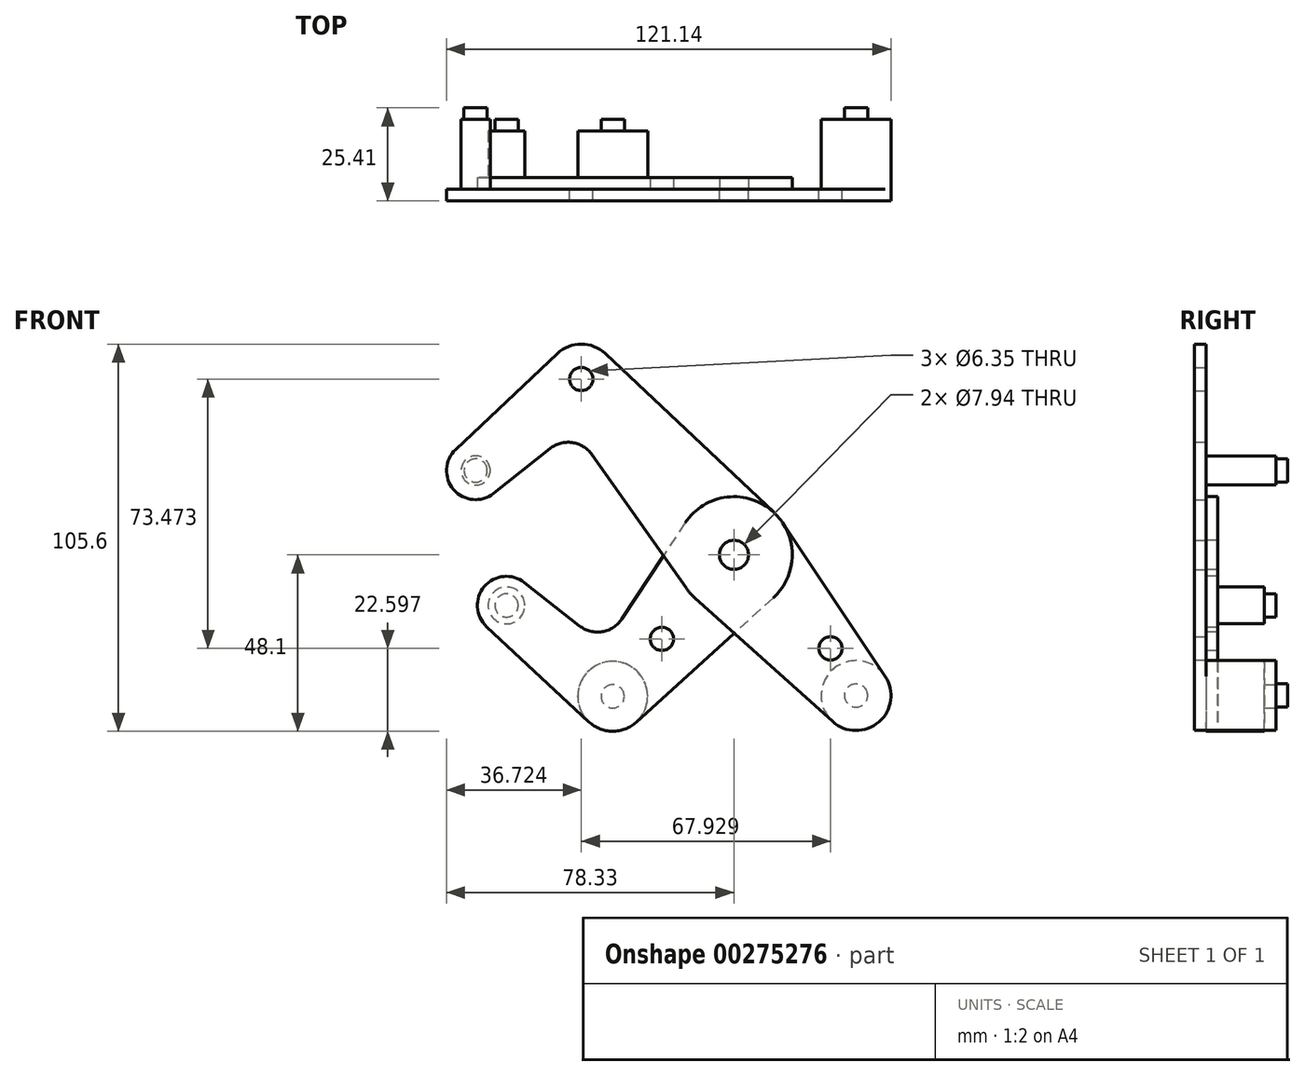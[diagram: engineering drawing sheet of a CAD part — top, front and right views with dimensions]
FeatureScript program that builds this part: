
annotation { "Feature Type Name" : "Feature", "Feature Type Description" : "" }
export const myFeature = defineFeature(function(context is Context, id is Id, definition is map)
    precondition{}
    {
        {
            var Q0;
            Q0=qCreatedBy(makeId("Front.planeOp"),FACE);
            var sketch = newSketch(context, id + "F0", { "sketchPlane" : qUnion([Q0])});
            skLineSegment(sketch, "E0", {"start": v(-41.6, 47.97) * mm, "end": v(41.6, -47.97) * mm, "construction": true});
            skCircle(sketch, "E1", {"center": v(0, 0) * mm, "radius": 3.18 * mm});
            skCircle(sketch, "E2", {"center": v(33.29, -38.38) * mm, "radius": 3.18 * mm});
            skCircle(sketch, "E3", {"center": v(-41.6, 47.97) * mm, "radius": 3.18 * mm});
            skCircle(sketch, "E4", {"center": v(-70.39, 23) * mm, "radius": 3.18 * mm});
            skLineSegment(sketch, "E5", {"start": v(-41.6, 47.97) * mm, "end": v(-70.39, 23) * mm, "construction": true});
            skCircle(sketch, "E6", {"center": v(33.29, -38.38) * mm, "radius": 9.53 * mm});
            skCircle(sketch, "E7", {"center": v(-70.39, 23) * mm, "radius": 7.94 * mm});
            skCircle(sketch, "E8", {"center": v(-41.6, 47.97) * mm, "radius": 9.53 * mm});
            skLineSegment(sketch, "E9", {"start": v(-75.83, 28.78) * mm, "end": v(-48.14, 54.9) * mm});
            skLineSegment(sketch, "E10", {"start": v(-65.44, 16.8) * mm, "end": v(-50.15, 28.98) * mm});
            skCircle(sketch, "E11", {"center": v(0, 0) * mm, "radius": 15.88 * mm});
            skLineSegment(sketch, "E12", {"start": v(-35.07, 54.9) * mm, "end": v(10.9, 11.55) * mm});
            skLineSegment(sketch, "E13", {"start": v(-38.72, 27.35) * mm, "end": v(-12.97, -9.15) * mm});
            skLineSegment(sketch, "E14", {"start": v(-10.6, -11.82) * mm, "end": v(26.93, -45.47) * mm});
            skLineSegment(sketch, "E15", {"start": v(13.2, 8.82) * mm, "end": v(41.2, -33.08) * mm});
            skArc(sketch, "E16.filletArc", {"start": v(-38.72, 27.35) * mm, "mid": v(-44.08, 30.63) * mm, "end": v(-50.15, 28.98) * mm});
            skLineSegment(sketch, "E17", {"start": v(0, 0) * mm, "end": v(-33.05, -38.58) * mm, "construction": true});
            skLineSegment(sketch, "E18", {"start": v(-33.05, -38.58) * mm, "end": v(-61.98, -13.8) * mm, "construction": true});
            skCircle(sketch, "E19", {"center": v(-61.98, -13.8) * mm, "radius": 3.18 * mm});
            skCircle(sketch, "E20", {"center": v(-33.05, -38.58) * mm, "radius": 3.18 * mm});
            skCircle(sketch, "E21", {"center": v(-61.98, -13.8) * mm, "radius": 7.94 * mm});
            skCircle(sketch, "E22", {"center": v(-33.05, -38.58) * mm, "radius": 9.53 * mm});
            skLineSegment(sketch, "E23", {"start": v(-57.08, -7.55) * mm, "end": v(-42.08, -19.35) * mm});
            skLineSegment(sketch, "E24", {"start": v(-67.4, -19.6) * mm, "end": v(-39.54, -45.55) * mm});
            skLineSegment(sketch, "E25", {"start": v(-13.25, 8.74) * mm, "end": v(-30.55, -17.48) * mm});
            skLineSegment(sketch, "E26", {"start": v(10.67, -11.75) * mm, "end": v(-26.65, -45.63) * mm});
            skArc(sketch, "E27.filletArc", {"start": v(-42.08, -19.35) * mm, "mid": v(-35.9, -20.95) * mm, "end": v(-30.55, -17.48) * mm});
            skCircle(sketch, "E28", {"center": v(-19.62, -22.9) * mm, "radius": 3.18 * mm});
            skCircle(sketch, "E29", {"center": v(26.32, -25.5) * mm, "radius": 3.18 * mm});
            skLineSegment(sketch, "E30", {"start": v(26.32, -25.5) * mm, "end": v(23.92, -27.58) * mm, "construction": true});
            skCircle(sketch, "E31", {"center": v(0, 0) * mm, "radius": 3.97 * mm});
            skSolve(sketch);
        }
        {
            var Q0;
            Q0=qCreatedBy(makeId("Front.planeOp"),FACE);
            cPlane(context, id + "F1", {"entities" : qUnion([Q0]), "cplaneType" : CPlaneType.OFFSET, "offset" : 9.52 * mm, "oppositeDirection" : true, "width" : 254 * mm, "height" : 254 * mm});
        }
        {
            var Q0;
            Q0=makeQuery(id+"F0.imprint","IMPRINT",FACE,{"disambiguationData":[TD([[makeQuery(id+"F0.imprint","IMPRINT",EDGE,{"derivedFrom":sQuery(id+"F0.wireOp",EDGE,"E2")}),-1.0]])]});
            var Q1;
            Q1=makeQuery(id+"F0.imprint","IMPRINT",FACE,{"disambiguationData":[TD([[makeQuery(id+"F0.imprint","IMPRINT",EDGE,{"derivedFrom":sQuery(id+"F0.wireOp",EDGE,"E3")}),-1.0]])]});
            var Q2;
            Q2=makeQuery(id+"F0.imprint","IMPRINT",FACE,{"disambiguationData":[TD([[makeQuery(id+"F0.imprint","IMPRINT",EDGE,{"derivedFrom":sQuery(id+"F0.wireOp",EDGE,"E4")}),-1.0]])]});
            var Q3;
            {var subQ0=sQuery(id+"F0.wireOp",EDGE,"E13");var subQ1=sQuery(id+"F0.wireOp",EDGE,"E11");var subQ2=makeQuery(id+"F0.imprint","INTERSECT",VERTEX,{"derivedFrom":[subQ1,subQ0]});Q3=makeQuery(id+"F0.imprint","IMPRINT",FACE,{"disambiguationData":[TD([[makeQuery(id+"F0.imprint","IMPRINT",EDGE,{"disambiguationData":[TD([[subQ2,1.0]])],"derivedFrom":subQ1}),-1.0]])]});}
            var Q4;
            {var subQ0=sQuery(id+"F0.wireOp",EDGE,"E14");var subQ1=sQuery(id+"F0.wireOp",EDGE,"E11");var subQ2=makeQuery(id+"F0.imprint","INTERSECT",VERTEX,{"derivedFrom":[subQ1,subQ0]});Q4=makeQuery(id+"F0.imprint","IMPRINT",FACE,{"disambiguationData":[TD([[makeQuery(id+"F0.imprint","IMPRINT",EDGE,{"disambiguationData":[TD([[subQ2,-1.0]])],"derivedFrom":subQ1}),-1.0]])]});}
            var Q5;
            {var subQ0=sQuery(id+"F0.wireOp",EDGE,"E15");Q5=makeQuery(id+"F0.imprint","IMPRINT",FACE,{"disambiguationData":[TD([[makeQuery(id+"F0.imprint","IMPRINT",EDGE,{"derivedFrom":subQ0}),-1.0]])]});}
            var Q6;
            {var subQ1=sQuery(id+"F0.wireOp",EDGE,"E9");Q6=makeQuery(id+"F0.imprint","IMPRINT",FACE,{"disambiguationData":[TD([[makeQuery(id+"F0.imprint","IMPRINT",EDGE,{"derivedFrom":subQ1}),-1.0]])]});}
            var Q7;
            Q7=makeQuery(id+"F0.imprint","IMPRINT",FACE,{"disambiguationData":[TD([[makeQuery(id+"F0.imprint","IMPRINT",EDGE,{"derivedFrom":sQuery(id+"F0.wireOp",EDGE,"E31")}),-1.0]])]});
            extrude(context, id + "F2", {"entities" : qUnion([Q0, Q1, Q2, Q3, Q4, Q5, Q6, Q7]), "depth" : 3.17 * mm});
        }
        {
            var Q0;
            Q0=makeQuery(id+"F0.imprint","IMPRINT",FACE,{"disambiguationData":[TD([[makeQuery(id+"F0.imprint","IMPRINT",EDGE,{"derivedFrom":sQuery(id+"F0.wireOp",EDGE,"E31")}),-1.0]])]});
            var Q1;
            {var subQ0=sQuery(id+"F0.wireOp",EDGE,"E14");var subQ1=sQuery(id+"F0.wireOp",EDGE,"E11");var subQ2=makeQuery(id+"F0.imprint","INTERSECT",VERTEX,{"derivedFrom":[subQ1,subQ0]});Q1=makeQuery(id+"F0.imprint","IMPRINT",FACE,{"disambiguationData":[TD([[makeQuery(id+"F0.imprint","IMPRINT",EDGE,{"disambiguationData":[TD([[subQ2,-1.0]])],"derivedFrom":subQ1}),-1.0]])]});}
            var Q2;
            {var subQ0=sQuery(id+"F0.wireOp",EDGE,"E13");var subQ1=sQuery(id+"F0.wireOp",EDGE,"E11");var subQ2=makeQuery(id+"F0.imprint","INTERSECT",VERTEX,{"derivedFrom":[subQ1,subQ0]});Q2=makeQuery(id+"F0.imprint","IMPRINT",FACE,{"disambiguationData":[TD([[makeQuery(id+"F0.imprint","IMPRINT",EDGE,{"disambiguationData":[TD([[subQ2,1.0]])],"derivedFrom":subQ1}),-1.0]])]});}
            var Q3;
            {var subQ10=sQuery(id+"F0.wireOp",EDGE,"E23");Q3=makeQuery(id+"F0.imprint","IMPRINT",FACE,{"disambiguationData":[TD([[makeQuery(id+"F0.imprint","IMPRINT",EDGE,{"derivedFrom":subQ10}),-1.0]])]});}
            var Q4;
            Q4=makeQuery(id+"F0.imprint","IMPRINT",FACE,{"disambiguationData":[TD([[makeQuery(id+"F0.imprint","IMPRINT",EDGE,{"derivedFrom":sQuery(id+"F0.wireOp",EDGE,"E20")}),-1.0]])]});
            var Q5;
            Q5=makeQuery(id+"F0.imprint","IMPRINT",FACE,{"disambiguationData":[TD([[makeQuery(id+"F0.imprint","IMPRINT",EDGE,{"derivedFrom":sQuery(id+"F0.wireOp",EDGE,"E19")}),-1.0]])]});
            extrude(context, id + "F3", {"entities" : qUnion([Q0, Q1, Q2, Q3, Q4, Q5]), "oppositeDirection" : true, "depth" : 3.17 * mm});
        }
        {
            var Q0;
            Q0=makeQuery(id+"F2.opExtrude","CAP_FACE",FACE,{"disambiguationData":[OSD([sQuery(id+"F0.wireOp",EDGE,"E2"),sQuery(id+"F0.wireOp",EDGE,"E3"),sQuery(id+"F0.wireOp",EDGE,"E4"),sQuery(id+"F0.wireOp",EDGE,"E6"),sQuery(id+"F0.wireOp",EDGE,"E7"),sQuery(id+"F0.wireOp",EDGE,"E8"),sQuery(id+"F0.wireOp",EDGE,"E9"),sQuery(id+"F0.wireOp",EDGE,"E10"),sQuery(id+"F0.wireOp",EDGE,"E11"),sQuery(id+"F0.wireOp",EDGE,"E12"),sQuery(id+"F0.wireOp",EDGE,"E13"),sQuery(id+"F0.wireOp",EDGE,"E14"),sQuery(id+"F0.wireOp",EDGE,"E15"),sQuery(id+"F0.wireOp",EDGE,"E16.filletArc"),sQuery(id+"F0.wireOp",EDGE,"E29"),sQuery(id+"F0.wireOp",EDGE,"E31")])],"isStart":false});
            var sketch = newSketch(context, id + "F4", { "sketchPlane" : qUnion([Q0])});
            skCircle(sketch, "E32", {"center": v(33.29, -38.38) * mm, "radius": 9.53 * mm});
            skCircle(sketch, "E33", {"center": v(-70.39, 23) * mm, "radius": 3.98 * mm});
            skSolve(sketch);
        }
        {
            var Q0;
            Q0=makeQuery(id+"F3.opExtrude","CAP_FACE",FACE,{"disambiguationData":[OSD([sQuery(id+"F0.wireOp",EDGE,"E11"),sQuery(id+"F0.wireOp",EDGE,"E19"),sQuery(id+"F0.wireOp",EDGE,"E20"),sQuery(id+"F0.wireOp",EDGE,"E21"),sQuery(id+"F0.wireOp",EDGE,"E22"),sQuery(id+"F0.wireOp",EDGE,"E23"),sQuery(id+"F0.wireOp",EDGE,"E24"),sQuery(id+"F0.wireOp",EDGE,"E25"),sQuery(id+"F0.wireOp",EDGE,"E26"),sQuery(id+"F0.wireOp",EDGE,"E27.filletArc"),sQuery(id+"F0.wireOp",EDGE,"E28"),sQuery(id+"F0.wireOp",EDGE,"E31")])],"isStart":true});
            var sketch = newSketch(context, id + "F5", { "sketchPlane" : qUnion([Q0])});
            skCircle(sketch, "E34", {"center": v(-33.05, -38.58) * mm, "radius": 9.53 * mm});
            skCircle(sketch, "E35", {"center": v(-61.98, -13.8) * mm, "radius": 5.02 * mm});
            skSolve(sketch);
        }
        {
            var Q0;
            Q0 = qSketchRegion(id + "F4", true);
            var Q1;
            Q1 = qSketchRegion(id + "F5", true);
            var Q2;
            Q2=qCreatedBy(id+"F1.planeOp",FACE);
            extrude(context, id + "F6", {"entities" : qUnion([Q0, Q1]), "endBound" : BoundingType.UP_TO_SURFACE, "oppositeDirection" : true, "endBoundEntityFace" : qUnion([Q2]), "depth" : 25.4 * mm});
        }
        {
            var Q0;
            Q0=makeQuery(id+"F3.opExtrude","SWEPT_BODY",BODY,{"disambiguationData":[OSD([sQuery(id+"F0.wireOp",EDGE,"E11"),sQuery(id+"F0.wireOp",EDGE,"E19"),sQuery(id+"F0.wireOp",EDGE,"E20"),sQuery(id+"F0.wireOp",EDGE,"E21"),sQuery(id+"F0.wireOp",EDGE,"E22"),sQuery(id+"F0.wireOp",EDGE,"E23"),sQuery(id+"F0.wireOp",EDGE,"E24"),sQuery(id+"F0.wireOp",EDGE,"E25"),sQuery(id+"F0.wireOp",EDGE,"E26"),sQuery(id+"F0.wireOp",EDGE,"E27.filletArc"),sQuery(id+"F0.wireOp",EDGE,"E28"),sQuery(id+"F0.wireOp",EDGE,"E31")])]});
            var Q1;
            Q1=makeQuery(id+"F2.opExtrude","SWEPT_BODY",BODY,{"disambiguationData":[OSD([sQuery(id+"F0.wireOp",EDGE,"E2"),sQuery(id+"F0.wireOp",EDGE,"E3"),sQuery(id+"F0.wireOp",EDGE,"E4"),sQuery(id+"F0.wireOp",EDGE,"E6"),sQuery(id+"F0.wireOp",EDGE,"E7"),sQuery(id+"F0.wireOp",EDGE,"E8"),sQuery(id+"F0.wireOp",EDGE,"E9"),sQuery(id+"F0.wireOp",EDGE,"E10"),sQuery(id+"F0.wireOp",EDGE,"E11"),sQuery(id+"F0.wireOp",EDGE,"E12"),sQuery(id+"F0.wireOp",EDGE,"E13"),sQuery(id+"F0.wireOp",EDGE,"E14"),sQuery(id+"F0.wireOp",EDGE,"E15"),sQuery(id+"F0.wireOp",EDGE,"E16.filletArc"),sQuery(id+"F0.wireOp",EDGE,"E29"),sQuery(id+"F0.wireOp",EDGE,"E31")])]});
            var Q2;
            Q2=makeQuery(id+"F6.opExtrude","SWEPT_BODY",BODY,{"disambiguationData":[OSD([sQuery(id+"F4.wireOp",EDGE,"E32")])]});
            var Q3;
            Q3=makeQuery(id+"F6.opExtrude","SWEPT_BODY",BODY,{"disambiguationData":[OSD([sQuery(id+"F4.wireOp",EDGE,"E33")])]});
            var Q4;
            Q4=makeQuery(id+"F6.opExtrude","SWEPT_BODY",BODY,{"disambiguationData":[OSD([sQuery(id+"F5.wireOp",EDGE,"E34")])]});
            var Q5;
            Q5=makeQuery(id+"F6.opExtrude","SWEPT_BODY",BODY,{"disambiguationData":[OSD([sQuery(id+"F5.wireOp",EDGE,"E35")])]});
            booleanBodies(context, id + "F7", {"operationType" : BooleanOperationType.SUBTRACTION, "tools" : qUnion([Q0, Q1]), "targets" : qUnion([Q2, Q3, Q4, Q5]), "keepTools" : true});
        }
        {
            var Q0;
            Q0=makeQuery(id+"F6.opExtrude","SWEPT_BODY",BODY,{"disambiguationData":[OSD([sQuery(id+"F4.wireOp",EDGE,"E33")])]});
            var Q1;
            Q1=makeQuery(id+"F6.opExtrude","SWEPT_BODY",BODY,{"disambiguationData":[OSD([sQuery(id+"F5.wireOp",EDGE,"E35")])]});
            var Q2;
            Q2=makeQuery(id+"F6.opExtrude","SWEPT_BODY",BODY,{"disambiguationData":[OSD([sQuery(id+"F5.wireOp",EDGE,"E34")])]});
            var Q3;
            Q3=makeQuery(id+"F6.opExtrude","SWEPT_BODY",BODY,{"disambiguationData":[OSD([sQuery(id+"F4.wireOp",EDGE,"E32")])]});
            var Q4;
            Q4=qCreatedBy(id+"F1.planeOp",FACE);
            mirror(context, id + "F8", {"operationType" : NewBodyOperationType.ADD, "entities" : qUnion([Q0, Q1, Q2, Q3]), "mirrorPlane" : qUnion([Q4])});
        }
    });
